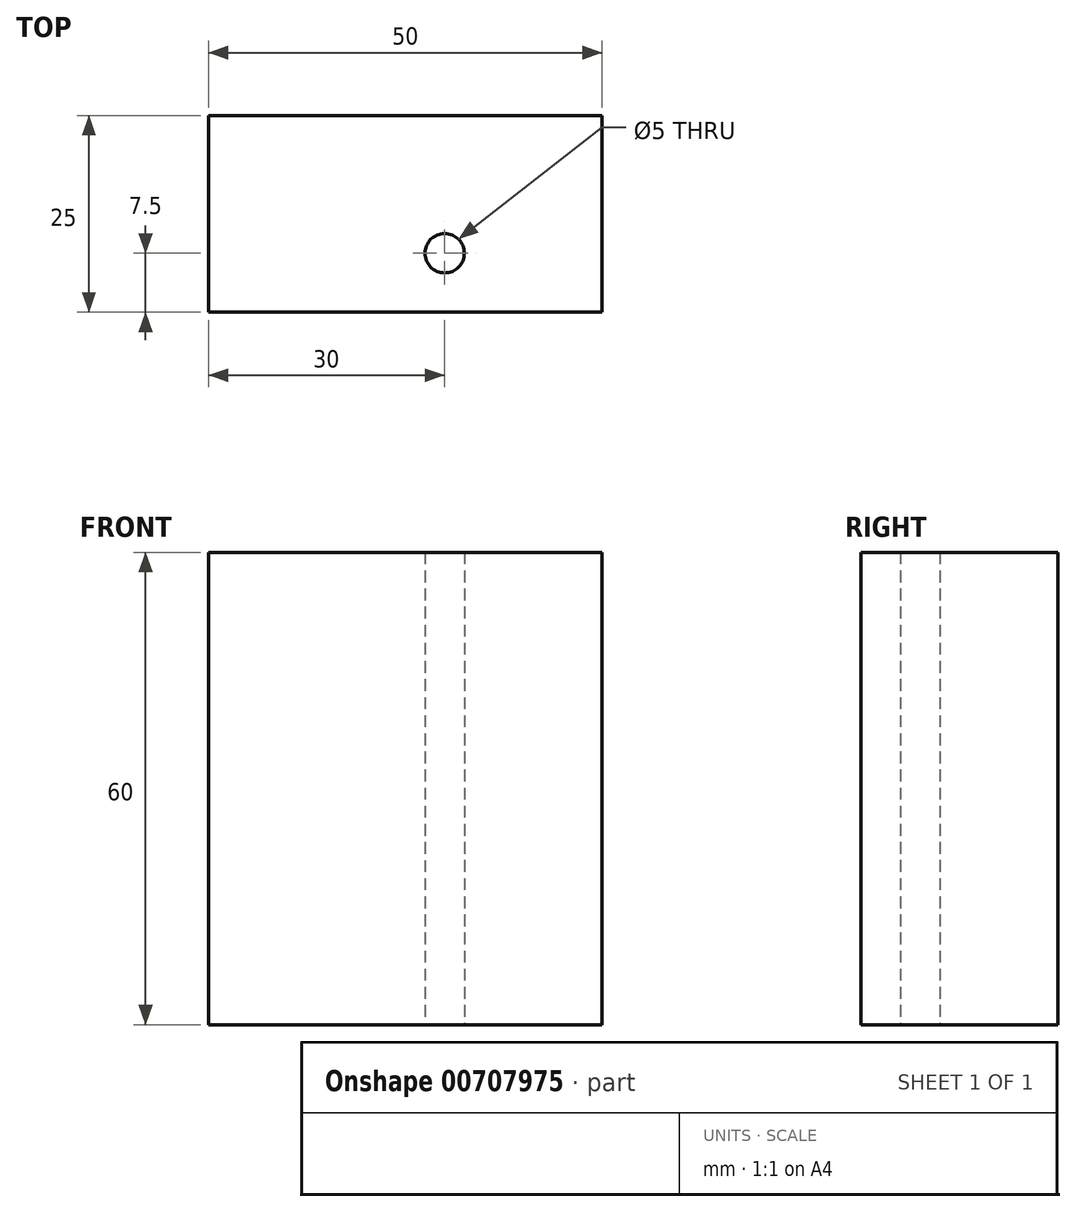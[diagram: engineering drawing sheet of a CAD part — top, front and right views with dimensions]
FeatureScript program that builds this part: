
annotation { "Feature Type Name" : "Feature", "Feature Type Description" : "" }
export const myFeature = defineFeature(function(context is Context, id is Id, definition is map)
    precondition{}
    {
        {
            var Q0;
            Q0=qCreatedBy(makeId("Front.planeOp"),FACE);
            var sketch = newSketch(context, id + "F0", { "sketchPlane" : qUnion([Q0])});
            skLineSegment(sketch, "E0.bottom", {"start": v(0, 0) * mm, "end": v(50, 0) * mm});
            skLineSegment(sketch, "E0.top", {"start": v(0, 60) * mm, "end": v(50, 60) * mm});
            skLineSegment(sketch, "E0.left", {"start": v(0, 0) * mm, "end": v(0, 60) * mm});
            skLineSegment(sketch, "E0.right", {"start": v(50, 0) * mm, "end": v(50, 60) * mm});
            skSolve(sketch);
        }
        {
            var Q0;
            Q0 = qSketchRegion(id + "F0", true);
            extrude(context, id + "F1", {"entities" : qUnion([Q0]), "endBound" : BoundingType.SYMMETRIC, "oppositeDirection" : true, "depth" : 25 * mm, "offsetDistance" : 25 * mm});
        }
        {
            var Q0;
            Q0=qCreatedBy(makeId("Right.planeOp"),FACE);
            var sketch = newSketch(context, id + "F2", { "sketchPlane" : qUnion([Q0])});
            skLineSegment(sketch, "E1", {"start": v(0, 60.61) * mm, "end": v(0, 70.61) * mm});
            skLineSegment(sketch, "E2", {"start": v(0, 70.61) * mm, "end": v(-12.12, 60.42) * mm});
            skLineSegment(sketch, "E3", {"start": v(-12.12, 60.42) * mm, "end": v(0, 60.61) * mm});
            skSolve(sketch);
        }
        {
            var Q0;
            Q0 = qSketchRegion(id + "FAi0KhsCUXn1voL_1", true);
            var Q1;
            Q1 = qSketchRegion(id + "F2", true);
            extrude(context, id + "F3", {"entities" : qUnion([Q0, Q1]), "operationType" : NewBodyOperationType.REMOVE, "endBound" : BoundingType.SYMMETRIC, "oppositeDirection" : true, "depth" : 25 * mm, "offsetDistance" : 25 * mm});
        }
        {
            var Q0;
            Q0=qCreatedBy(makeId("Top.planeOp"),FACE);
            var sketch = newSketch(context, id + "F4", { "sketchPlane" : qUnion([Q0])});
            skLineSegment(sketch, "E4", {"start": v(0, 0) * mm, "end": v(30, 0) * mm});
            skLineSegment(sketch, "E5", {"start": v(30, 0) * mm, "end": v(30, -5) * mm});
            skCircle(sketch, "E6", {"center": v(30, -5) * mm, "radius": 2.5 * mm});
            skSolve(sketch);
        }
        {
            var Q0;
            Q0 = qSketchRegion(id + "F4", true);
            extrude(context, id + "F5", {"entities" : qUnion([Q0]), "operationType" : NewBodyOperationType.REMOVE, "endBound" : BoundingType.UP_TO_NEXT, "depth" : 25 * mm, "offsetDistance" : 25 * mm});
        }
    });
